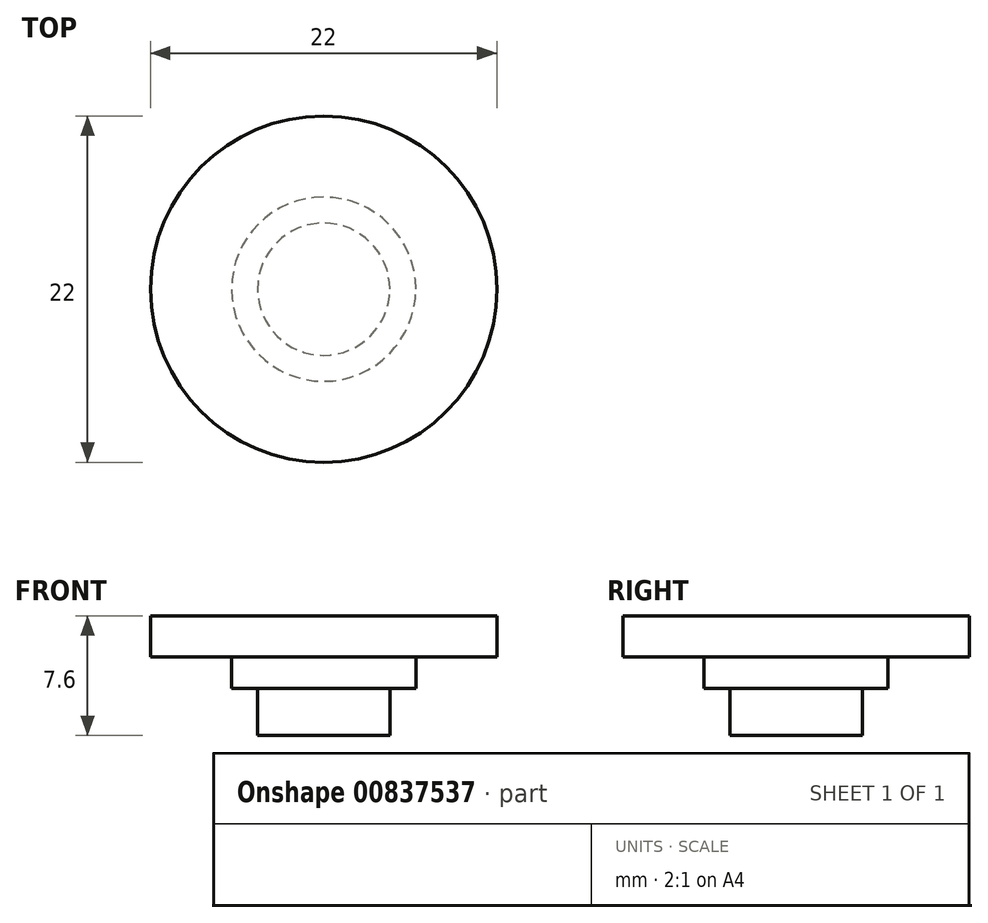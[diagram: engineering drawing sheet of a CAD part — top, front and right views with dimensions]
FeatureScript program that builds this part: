
annotation { "Feature Type Name" : "Feature", "Feature Type Description" : "" }
export const myFeature = defineFeature(function(context is Context, id is Id, definition is map)
    precondition{}
    {
        {
            var Q0;
            Q0=qCreatedBy(makeId("Front.planeOp"),FACE);
            var sketch = newSketch(context, id + "F0", { "sketchPlane" : qUnion([Q0])});
            skLineSegment(sketch, "E0", {"start": v(0, 8.98) * mm, "end": v(-11, 8.98) * mm});
            skLineSegment(sketch, "E1", {"start": v(-11, 8.98) * mm, "end": v(-11, 6.38) * mm});
            skLineSegment(sketch, "E2", {"start": v(-11, 6.38) * mm, "end": v(-5.85, 6.38) * mm});
            skLineSegment(sketch, "E3", {"start": v(-5.85, 6.38) * mm, "end": v(-5.85, 4.38) * mm});
            skLineSegment(sketch, "E4", {"start": v(-5.85, 4.38) * mm, "end": v(-4.2, 4.38) * mm});
            skLineSegment(sketch, "E5", {"start": v(-4.2, 4.38) * mm, "end": v(-4.2, 1.38) * mm});
            skLineSegment(sketch, "E6", {"start": v(-4.2, 1.38) * mm, "end": v(0, 1.38) * mm});
            skLineSegment(sketch, "E7", {"start": v(0, 1.38) * mm, "end": v(0, 8.98) * mm, "construction": true});
            skLineSegment(sketch, "E8", {"start": v(0, 8.98) * mm, "end": v(0, 1.38) * mm});
            skSolve(sketch);
        }
        {
            var Q0;
            Q0 = qSketchRegion(id + "F0", true);
            var Q1;
            Q1=sQuery(id+"F0.wireOp",EDGE,"E7");
            revolve(context, id + "F1", {"surfaceOperationType" : NewSurfaceOperationType.NEW, "entities" : qUnion([Q0]), "axis" : qUnion([Q1]), "revolveType" : RevolveType.FULL});
        }
    });
